# Revit family: TD92_OCT713_CON210_RVT20_R00
name_source: partatom
category: Mobiliário
units: mm (PartAtom-declared; Revit-internal decimal feet)

## family parameters
Com base no plano de trabalho = Não
Compartilhado = Não
Corte com vazios quando carregada = Não
Número OmniClass = 23.40.20.00
Ponto de cálculo do ambiente = Não
Sempre na vertical = Sim
Título OmniClass = General Furniture and Specialties

## types (1)
- TD92_OCT713_CON210_RVT20_R00
    Descrição = Quem poderia reunir, em uma só peça, beleza, requinte, sofisticação e conforto? É a Espreguiçadeira Tramontina Octo em Polietileno que nasceu para você relaxar, e ainda vai embelezar seu ambiente.
    Elevação padrão = 0  [stored 0 ft]
    Fabricante = Tramontina Delta S/A
    Modelo = Espreguiçadeira Tramontina Octo em Polietileno Concreto
    Nota-chave = 92713210
    URL = https://www.tramontinastore.com

note: [stored X ft] marks values corroborated as IEEE doubles in the binary element streams (Revit-internal decimal feet)
